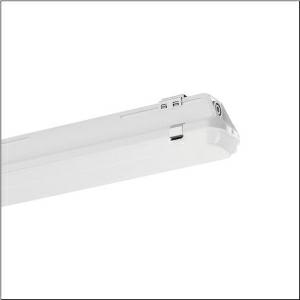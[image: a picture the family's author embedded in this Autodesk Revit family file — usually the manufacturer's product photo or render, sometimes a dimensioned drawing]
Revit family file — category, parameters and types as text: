
# Revit family: monsun_r__21_emergency_51fb10dp487c3h_1d8e
name_source: partatom
category: Lighting Fixtures
units: mm (PartAtom-declared; Revit-internal decimal feet)

## family parameters
Cut with Voids When Loaded = No
Host = Face
Light Source = No
Part Type = Normal
Room Calculation Point = No
Round Connector Dimension = Use Diameter
Shared = No

## types (1)
- --- (1 x LED, 8090 lm, 49.9 W, 4000K)
    Apparent Load = 50 VA
    CIE Flux Codes = 47 77 93 94 100
    Color Rendering = 80
    Color Temperature = 4000K
    Default Elevation = 1800 mm
    Description = Monsun® 21 emergency, damp-proof luminaire, chain hanger, primary optical cover: enclosure, of PMMA, light emission: direct distribution, primary light characteristic: symmetric, installation type: vertical mounting, horizontal mounting, surface-mounted, suspended mounting, LED, rated luminous flux: 8.090lm, luminous efficacy: 176lm/W, light colour: 840, colour temperature: 4000K, control gear: DALI 2, with terminal, 5+3-pole, max. 2.5mm², mains connection: 220..240V, AC, 50/60Hz, rated input power: 50W, control gear: single battery element, battery: LiFePO4, 9Ah, housing, of glass-fibre reinforced polyester, uncoated, bright grey, incl. chain hanger, length: 1.590mm, width: 90mm, height: 88mm, clip for enclosure, of stainless steel (V2A), ceiling mounting element, of stainless steel (V2A), chain hanger, of stainless steel (V2A), protection rating (complete): IP66, insulation class (complete): insulation class I (protective earthing), certification: CE, UKCA, protection symbol: D, impact resistance: IK04, permissible operating ambient temperature: +5..+25°C, standard: EN 50419, EN 60598-2-1, EN 60598-2-22, corresponds to IFS (International Featured Standards) requirements for safety and quality in the food industry, for indoor or canopied outdoor use, no direct snow, no direct sun, no direct rain, LABS conformity tested according to VDMA 24364:2018-05, contact your sales advisor before using the luminaires in applications with unclear chemical exposure, large temperature fluctuations or condensation-forming humidity, packaging unit: 1 piece
    Height = 89 mm
    Lamp = 1 x LED
    Lamp Light Flux = 8090 lm
    Lamp Power = 49.9 W
    Lamp count = 1
    Length = 1590 mm
    Luminous efficacy = 162 lm/W
    Manufacturer = Siteco
    ModVariant = No
    Model = 51FB10DP487C3H
    Mounting Place = Ceiling
    Mounting Type = Surface mounted
    Number of Poles = 1
    OnlyDefault = Yes
    Power Factor = 1
    Product Name = Monsun® 21 emergency
    Product group = damp-proof luminaire
    ProductGroupID = 301
    Protection Class = Protection class I
    Protection Degree = IP 66
    RLX_Detail_Level = 1
    RLX_Emergency_Light_Flux = 0 lm
    RLX_Emergency_Type = 0
    RLX_Emergency_Type_DB = No
    RlxData = <blob elided: 92733 chars, md5=1357f682>
    Socket = socket
    Standby Power = 0 W
    System Light Flux = 8090 lm
    System Power = 50 W
    Type Comments = : luminous flux: 100 % | dim-lin: 254 | 311 mA
    Type Image = l_1319656.jpg
    URL = http://relux.com
    VarID = @adj_051591
    Voltage = 0 V
    Weight = 0.00 kg
    Width = 90 mm

## geometry (parser evidence)
native form markers: Blend x4, Sweep x13
no freeform markers — native parametric forms only
